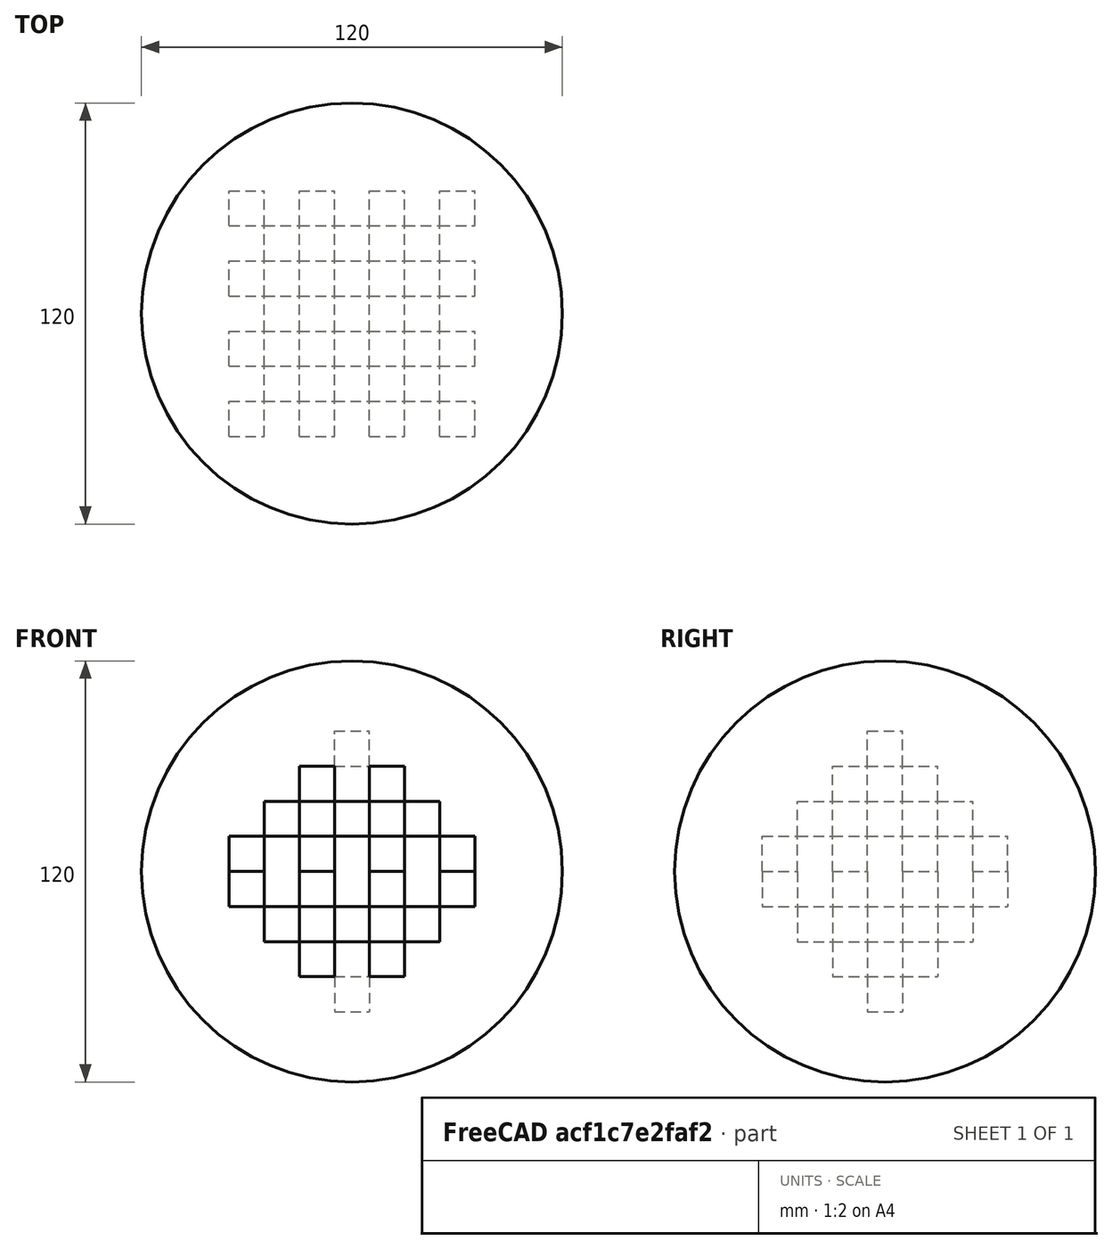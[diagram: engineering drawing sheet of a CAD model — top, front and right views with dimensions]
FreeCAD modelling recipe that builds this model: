
FCSTD DOCUMENT  (FreeCAD 1.0R39319 (Git))
Label: srodriguez_repte1
License: All rights reserved
LicenseURL: https://en.wikipedia.org/wiki/All_rights_reserved
objects: Part::Box×12, Part::FeaturePython×6, Part::Cut×4, Part::MultiFuse×2, Part::Sphere×1
note: 19 computed .brp shape members not serialized (recipe doc carries the construction recipe); baked Part::Feature solids carry a one-line shape summary decoded from their .brp

FEATURE [Part::Box] Box  label="Cube"
  AttacherType = Attacher::AttachEngine3D
  Height = 10
  Length = 10
  Width = 10
FEATURE [Part::FeaturePython] Array  # Draft array (typed FeaturePython)
  AlwaysSyncPlacement = false
  Angle = 360
  ArrayType = 0
  Axis = (0,0,1)
  Base = -> Box
  Center = (0,0,0)
  Count = 16
  ExpandArray = false
  Fuse = false
  IntervalAxis = (0,0,0)
  IntervalX = (20,0,0)
  IntervalY = (0,20,0)
  IntervalZ = (0,0,100)
  NumberCircles = 3
  NumberPolar = 5
  NumberX = 4
  NumberY = 4
  NumberZ = 1
  PlacementList = 16 placements: [(0,0,0),(0,20,0),(0,40,0),(0,60,0),(20,0,0),(20,20,0),(20,40,0),(20,60,0),(40,0,0),(40,20,0),(40,40,0),(40,60,0),(60,0,0),(60,20,0),(60,40,0),(60,60,0)]
  RadialDistance = 50
  ScaleList = (16) [(1,1,1),(1,1,1),(1,1,1),(1,1,1),(1,1,1),(1,1,1),(1,1,1),(1,1,1),(1,1,1),(1,1,1),(1,1,1),(1,1,1),(1,1,1),(1,1,1),(1,1,1),(1,1,1)]
  Symmetry = 1
  TangentialDistance = 25
FEATURE [Part::Box] Box001  label="Cube001"
  AttacherType = Attacher::AttachEngine3D
  Height = 10
  Length = 30
  Placement = pos=(20,20,0) rot=(0,0,1;0rad)
  Width = 30
FEATURE [Part::Cut] Cut
  Base = -> Array
  Refine = true
  Tool = -> Box001
FEATURE [Part::Box] Box002  label="Cube002"
  AttacherType = Attacher::AttachEngine3D
  Height = 10
  Length = 10
  Width = 10
FEATURE [Part::FeaturePython] Array001  # Draft array (typed FeaturePython)
  AlwaysSyncPlacement = false
  Angle = 360
  ArrayType = 0
  Axis = (0,0,1)
  Base = -> Box002
  Center = (0,0,0)
  Count = 9
  ExpandArray = false
  Fuse = false
  IntervalAxis = (0,0,0)
  IntervalX = (20,0,0)
  IntervalY = (0,20,0)
  IntervalZ = (0,0,100)
  NumberCircles = 3
  NumberPolar = 5
  NumberX = 3
  NumberY = 3
  NumberZ = 1
  Placement = pos=(10,10,10) rot=(0,0,1;0rad)
  PlacementList = 9 placements: [(0,0,0),(0,20,0),(0,40,0),(20,0,0),(20,20,0),(20,40,0),(40,0,0),(40,20,0),(40,40,0)]
  RadialDistance = 50
  ScaleList = (9) [(1,1,1),(1,1,1),(1,1,1),(1,1,1),(1,1,1),(1,1,1),(1,1,1),(1,1,1),(1,1,1)]
  Symmetry = 1
  TangentialDistance = 25
FEATURE [Part::Box] Box003  label="Cube003"
  AttacherType = Attacher::AttachEngine3D
  Height = 10
  Length = 10
  Placement = pos=(30,30,10) rot=(0,0,1;0rad)
  Width = 10
FEATURE [Part::Box] Box004  label="Cube004"
  AttacherType = Attacher::AttachEngine3D
  Height = 10
  Length = 10
  Width = 10
FEATURE [Part::FeaturePython] Array002  # Draft array (typed FeaturePython)
  AlwaysSyncPlacement = false
  Angle = 360
  ArrayType = 0
  Axis = (0,0,1)
  Base = -> Box004
  Center = (0,0,0)
  Count = 4
  ExpandArray = false
  Fuse = false
  IntervalAxis = (0,0,0)
  IntervalX = (20,0,0)
  IntervalY = (0,20,0)
  IntervalZ = (0,0,100)
  NumberCircles = 3
  NumberPolar = 5
  NumberX = 2
  NumberY = 2
  NumberZ = 1
  Placement = pos=(20,20,20) rot=(0,0,1;0rad)
  PlacementList = 4 placements: [(0,0,0),(0,20,0),(20,0,0),(20,20,0)]
  RadialDistance = 50
  ScaleList = (4) [(1,1,1),(1,1,1),(1,1,1),(1,1,1)]
  Symmetry = 1
  TangentialDistance = 25
FEATURE [Part::Cut] Cut001
  Base = -> Array001
  Refine = true
  Tool = -> Box003
FEATURE [Part::Box] Box005  label="Cube005"
  AttacherType = Attacher::AttachEngine3D
  Height = 10
  Length = 10
  Placement = pos=(30,30,30) rot=(0,0,1;0rad)
  Width = 10
FEATURE [Part::MultiFuse] Fusion  label="Piràmide_vermella"
  Refine = true
  Shapes = -> [Box005,Cut001,Array002,Cut]
FEATURE [Part::Box] Box006  label="Cube006"
  AttacherType = Attacher::AttachEngine3D
  Height = 10
  Length = 10
  Width = 10
FEATURE [Part::FeaturePython] Array003  # Draft array (typed FeaturePython)
  AlwaysSyncPlacement = false
  Angle = 360
  ArrayType = 0
  Axis = (0,0,1)
  Base = -> Box006
  Center = (0,0,0)
  Count = 16
  ExpandArray = false
  Fuse = false
  IntervalAxis = (0,0,0)
  IntervalX = (20,0,0)
  IntervalY = (0,20,0)
  IntervalZ = (0,0,100)
  NumberCircles = 3
  NumberPolar = 5
  NumberX = 4
  NumberY = 4
  NumberZ = 1
  PlacementList = 16 placements: [(0,0,0),(0,20,0),(0,40,0),(0,60,0),(20,0,0),(20,20,0),(20,40,0),(20,60,0),(40,0,0),(40,20,0),(40,40,0),(40,60,0),(60,0,0),(60,20,0),(60,40,0),(60,60,0)]
  RadialDistance = 50
  ScaleList = (16) [(1,1,1),(1,1,1),(1,1,1),(1,1,1),(1,1,1),(1,1,1),(1,1,1),(1,1,1),(1,1,1),(1,1,1),(1,1,1),(1,1,1),(1,1,1),(1,1,1),(1,1,1),(1,1,1)]
  Symmetry = 1
  TangentialDistance = 25
FEATURE [Part::Box] Box007  label="Cube007"
  AttacherType = Attacher::AttachEngine3D
  Height = 10
  Length = 30
  Placement = pos=(20,20,0) rot=(0,0,1;0rad)
  Width = 30
FEATURE [Part::Box] Box008  label="Cube008"
  AttacherType = Attacher::AttachEngine3D
  Height = 10
  Length = 10
  Width = 10
FEATURE [Part::FeaturePython] Array004  # Draft array (typed FeaturePython)
  AlwaysSyncPlacement = false
  Angle = 360
  ArrayType = 0
  Axis = (0,0,1)
  Base = -> Box008
  Center = (0,0,0)
  Count = 9
  ExpandArray = false
  Fuse = false
  IntervalAxis = (0,0,0)
  IntervalX = (20,0,0)
  IntervalY = (0,20,0)
  IntervalZ = (0,0,100)
  NumberCircles = 3
  NumberPolar = 5
  NumberX = 3
  NumberY = 3
  NumberZ = 1
  Placement = pos=(10,10,10) rot=(0,0,1;0rad)
  PlacementList = 9 placements: [(0,0,0),(0,20,0),(0,40,0),(20,0,0),(20,20,0),(20,40,0),(40,0,0),(40,20,0),(40,40,0)]
  RadialDistance = 50
  ScaleList = (9) [(1,1,1),(1,1,1),(1,1,1),(1,1,1),(1,1,1),(1,1,1),(1,1,1),(1,1,1),(1,1,1)]
  Symmetry = 1
  TangentialDistance = 25
FEATURE [Part::Box] Box009  label="Cube009"
  AttacherType = Attacher::AttachEngine3D
  Height = 10
  Length = 10
  Placement = pos=(30,30,10) rot=(0,0,1;0rad)
  Width = 10
FEATURE [Part::Box] Box010  label="Cube010"
  AttacherType = Attacher::AttachEngine3D
  Height = 10
  Length = 10
  Width = 10
FEATURE [Part::FeaturePython] Array005  # Draft array (typed FeaturePython)
  AlwaysSyncPlacement = false
  Angle = 360
  ArrayType = 0
  Axis = (0,0,1)
  Base = -> Box010
  Center = (0,0,0)
  Count = 4
  ExpandArray = false
  Fuse = false
  IntervalAxis = (0,0,0)
  IntervalX = (20,0,0)
  IntervalY = (0,20,0)
  IntervalZ = (0,0,100)
  NumberCircles = 3
  NumberPolar = 5
  NumberX = 2
  NumberY = 2
  NumberZ = 1
  Placement = pos=(20,20,20) rot=(0,0,1;0rad)
  PlacementList = 4 placements: [(0,0,0),(0,20,0),(20,0,0),(20,20,0)]
  RadialDistance = 50
  ScaleList = (4) [(1,1,1),(1,1,1),(1,1,1),(1,1,1)]
  Symmetry = 1
  TangentialDistance = 25
FEATURE [Part::Box] Box011  label="Cube011"
  AttacherType = Attacher::AttachEngine3D
  Height = 10
  Length = 10
  Placement = pos=(30,30,30) rot=(0,0,1;0rad)
  Width = 10
FEATURE [Part::Cut] Cut002
  Base = -> Array003
  Refine = true
  Tool = -> Box007
FEATURE [Part::Cut] Cut003
  Base = -> Array004
  Refine = true
  Tool = -> Box009
FEATURE [Part::MultiFuse] Fusion001  label="Piràmide_groga"
  Placement = pos=(0,0,0) rot=(20,20,0;-3.14159rad)
  Refine = true
  Shapes = -> [Box011,Cut003,Array005,Cut002]
FEATURE [Part::Sphere] Sphere  label="Esfera buida"
  Angle1 = -90
  Angle2 = 90
  Angle3 = 360
  AttacherType = Attacher::AttachEngine3D
  Placement = pos=(35,35,0) rot=(0,0,1;0rad)
  Radius = 60
